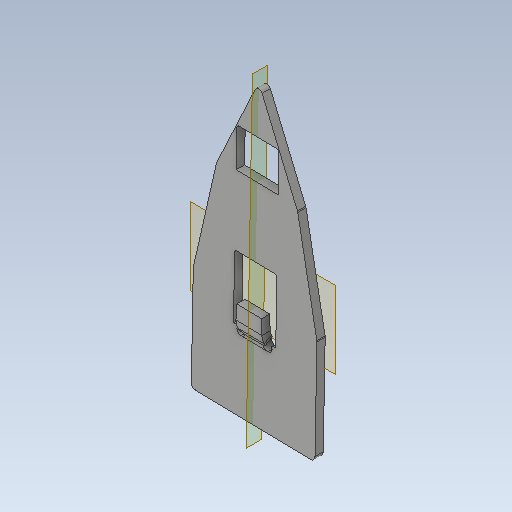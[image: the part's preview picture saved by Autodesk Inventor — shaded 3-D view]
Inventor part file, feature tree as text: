
AUTODESK INVENTOR PART (.ipt)
format: ipt  version: 2020.1 (Build 241239000, 239)  size: 407,040 bytes
history: native  units: mm
features: other x8, sheet_metal_op x3, sketch x3, hole x2, plane x1, fillet x1, reference x1
ambient origin geometry x8: Origin, YZ Plane, XZ Plane, XY Plane, X Axis, Y Axis, Z Axis, Center Point
bodies: Solid1 (feature_tree)
feature tree (19):
  plane  "Work Plane1"
  sheet_metal_op  "Face1"
  hole  "Hole1"  [1 undecoded]
  hole  "Hole2"  [1 undecoded]
  fillet  "Fillet1"  Radius=38.0mm
  sheet_metal_op  "Fold1"
  sheet_metal_op  "Fold2"
  other  "modtplan"
  sketch  "Sketch1"  dims[d0=8.0mm]
  other  "Plate1"
  reference  "Reference38"
  sketch  "Sketch2"  dims[d1=44.0mm d3=24.0mm d4=38.0mm d5=24.0mm d7=28.0mm d8=2.0mm]
  sketch  "Sketch3"  dims[d9=41.0mm d10=24.0mm d11=38.0mm d12=24.0mm d13=26.0mm d14=2.0mm d22=130.0mm d23=40.5mm d24=38.0mm d25=2.0mm d28=3.0mm d29=0.0mm d30=3.0mm d31=8.0mm d32=6.0mm d33=4.0mm d34=2.0mm d35=90.0deg d36=8.0mm d37=20.594885mm d38=0.0mm d39=3.0mm d40=8.0mm d41=6.0mm d42=4.0mm d43=2.0mm d44=90.0deg d45=8.0mm d46=20.594885mm d47=1.0mm d48=8.0mm d49=4.0mm d50=16.0mm d51=8.0mm d52=30.0deg d53=8.0mm d54=20.0mm d55=8.0mm d56=4.0mm d57=16.0mm d58=8.0mm d59=30.0deg d60=8.0mm]
  parser-record x2  (decoder bookkeeping rows leaked as tree rows — omitted from the tree; the rows remain in map.json)
  other  "modul top.iam"
  other  "vange top:1"
  other  "Definition1"
  other  "plade:1"
note: 2 required parameter values undecoded (feature->parameter linkage not recoverable at this tier; creation-order binding heuristic only, values carry confidence <= 0.55)
note: 2 file-system paths scrubbed to <path> (originals preserved in map.json)
